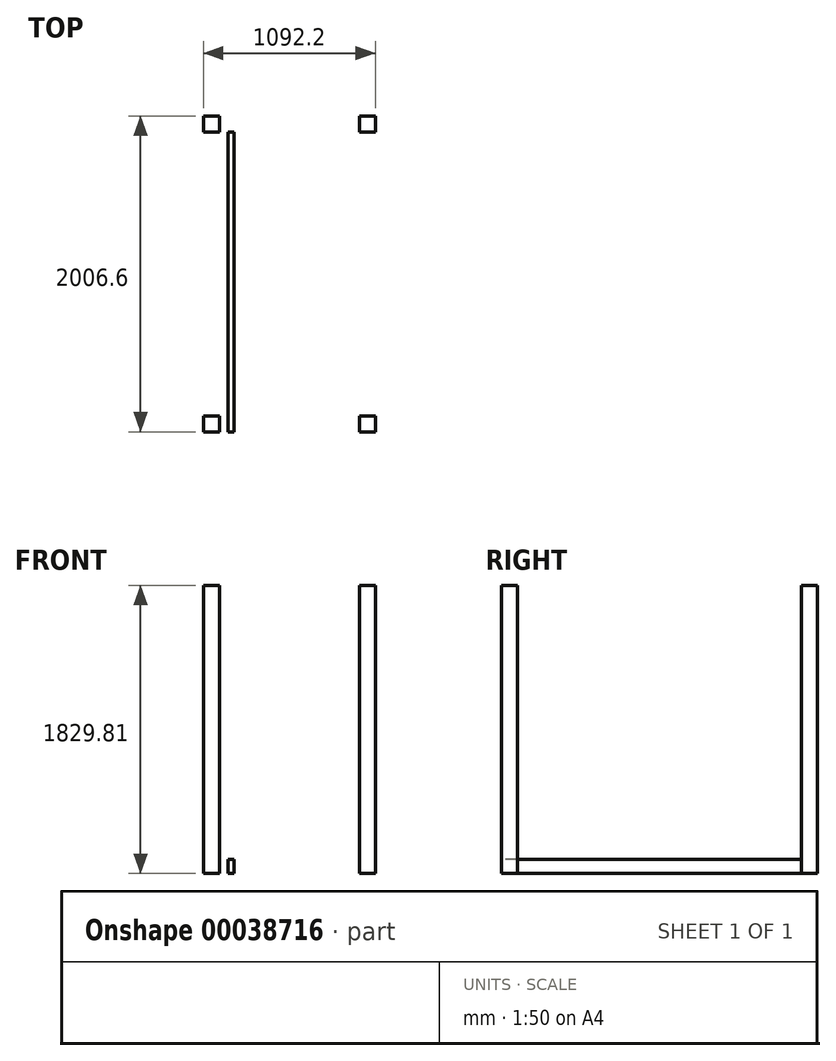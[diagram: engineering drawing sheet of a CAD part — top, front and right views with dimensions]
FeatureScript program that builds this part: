
annotation { "Feature Type Name" : "Feature", "Feature Type Description" : "" }
export const myFeature = defineFeature(function(context is Context, id is Id, definition is map)
    precondition{}
    {
        {
            var Q0;
            Q0=qCreatedBy(makeId("Top.planeOp"),FACE);
            var sketch = newSketch(context, id + "F0", { "sketchPlane" : qUnion([Q0])});
            skLineSegment(sketch, "E0.bottom", {"start": v(0, 0) * mm, "end": v(101.6, 0) * mm});
            skLineSegment(sketch, "E0.top", {"start": v(0, 101.6) * mm, "end": v(101.6, 101.6) * mm});
            skLineSegment(sketch, "E0.left", {"start": v(0, 0) * mm, "end": v(0, 101.6) * mm});
            skLineSegment(sketch, "E0.right", {"start": v(101.6, 0) * mm, "end": v(101.6, 101.6) * mm});
            skSolve(sketch);
        }
        {
            var Q0;
            Q0 = qSketchRegion(id + "F0", true);
            extrude(context, id + "F1", {"entities" : qUnion([Q0]), "depth" : 1828.8 * mm});
        }
        {
            var Q0;
            Q0=makeQuery(id+"F1.opExtrude","SWEPT_BODY",BODY,{"disambiguationData":[OSD([sQuery(id+"F0.wireOp",EDGE,"E0.bottom"),sQuery(id+"F0.wireOp",EDGE,"E0.top"),sQuery(id+"F0.wireOp",EDGE,"E0.left"),sQuery(id+"F0.wireOp",EDGE,"E0.right")])]});
            transform(context, id + "F2", {"entities" : qUnion([Q0]), "transformType" : TransformType.TRANSLATION_3D, "dx" : 0 * mm, "dy" : 0 * mm, "dz" : 0 * mm, "makeCopy" : true});
        }
        {
            var Q0;
            Q0=makeQuery(id+"F1.opExtrude","SWEPT_BODY",BODY,{"disambiguationData":[OSD([sQuery(id+"F0.wireOp",EDGE,"E0.bottom"),sQuery(id+"F0.wireOp",EDGE,"E0.top"),sQuery(id+"F0.wireOp",EDGE,"E0.left"),sQuery(id+"F0.wireOp",EDGE,"E0.right")])]});
            transform(context, id + "F3", {"entities" : qUnion([Q0]), "transformType" : TransformType.TRANSLATION_3D, "dx" : 990.6 * mm, "dy" : 1905 * mm, "dz" : 0 * mm, "makeCopy" : true});
        }
        {
            var Q0;
            Q0=makeQuery(id+"F1.opExtrude","SWEPT_BODY",BODY,{"disambiguationData":[OSD([sQuery(id+"F0.wireOp",EDGE,"E0.bottom"),sQuery(id+"F0.wireOp",EDGE,"E0.top"),sQuery(id+"F0.wireOp",EDGE,"E0.left"),sQuery(id+"F0.wireOp",EDGE,"E0.right")])]});
            transform(context, id + "F4", {"entities" : qUnion([Q0]), "transformType" : TransformType.TRANSLATION_3D, "dx" : 990.6 * mm, "dy" : 0 * mm, "dz" : 0 * mm, "makeCopy" : true});
        }
        {
            var Q0;
            Q0=makeQuery(id+"F2.opPattern","COPY",BODY,{"derivedFrom":makeQuery(id+"F1.opExtrude","SWEPT_BODY",BODY,{"disambiguationData":[OSD([sQuery(id+"F0.wireOp",EDGE,"E0.bottom"),sQuery(id+"F0.wireOp",EDGE,"E0.top"),sQuery(id+"F0.wireOp",EDGE,"E0.left"),sQuery(id+"F0.wireOp",EDGE,"E0.right")])]}),"instanceName":"1"});
            var Q1;
            Q1=makeQuery(id+"F1.opExtrude","SWEPT_BODY",BODY,{"disambiguationData":[OSD([sQuery(id+"F0.wireOp",EDGE,"E0.bottom"),sQuery(id+"F0.wireOp",EDGE,"E0.top"),sQuery(id+"F0.wireOp",EDGE,"E0.left"),sQuery(id+"F0.wireOp",EDGE,"E0.right")])]});
            transform(context, id + "F5", {"entities" : qUnion([Q0, Q1]), "transformType" : TransformType.TRANSLATION_3D, "dx" : 0 * mm, "dy" : 1905 * mm, "dz" : 0 * mm, "makeCopy" : true});
        }
        {
            var Q0;
            Q0=makeQuery(id+"F2.opPattern","COPY",BODY,{"derivedFrom":makeQuery(id+"F1.opExtrude","SWEPT_BODY",BODY,{"disambiguationData":[OSD([sQuery(id+"F0.wireOp",EDGE,"E0.bottom"),sQuery(id+"F0.wireOp",EDGE,"E0.top"),sQuery(id+"F0.wireOp",EDGE,"E0.left"),sQuery(id+"F0.wireOp",EDGE,"E0.right")])]}),"instanceName":"1"});
            deleteBodies(context, id + "F6", {"entities" : qUnion([Q0])});
        }
        {
            var Q0;
            Q0=makeQuery(id+"F5.opPattern","COPY",BODY,{"derivedFrom":makeQuery(id+"F2.opPattern","COPY",BODY,{"derivedFrom":makeQuery(id+"F1.opExtrude","SWEPT_BODY",BODY,{"disambiguationData":[OSD([sQuery(id+"F0.wireOp",EDGE,"E0.bottom"),sQuery(id+"F0.wireOp",EDGE,"E0.top"),sQuery(id+"F0.wireOp",EDGE,"E0.left"),sQuery(id+"F0.wireOp",EDGE,"E0.right")])]}),"instanceName":"1"}),"instanceName":"1"});
            deleteBodies(context, id + "F7", {"entities" : qUnion([Q0])});
        }
        {
            var Q0;
            Q0=qCreatedBy(makeId("Front.planeOp"),FACE);
            var sketch = newSketch(context, id + "F8", { "sketchPlane" : qUnion([Q0])});
            skLineSegment(sketch, "E1.bottom", {"start": v(156.86, 87.9) * mm, "end": v(194.96, 87.9) * mm});
            skLineSegment(sketch, "E1.top", {"start": v(156.86, -1) * mm, "end": v(194.96, -1) * mm});
            skLineSegment(sketch, "E1.left", {"start": v(156.86, 87.9) * mm, "end": v(156.86, -1) * mm});
            skLineSegment(sketch, "E1.right", {"start": v(194.96, 87.9) * mm, "end": v(194.96, -1) * mm});
            skSolve(sketch);
        }
        {
            var Q0;
            Q0 = qSketchRegion(id + "F8", true);
            extrude(context, id + "F9", {"entities" : qUnion([Q0]), "oppositeDirection" : true, "depth" : 1905 * mm});
        }
    });
